# Revit family: EVC-1122-VI
name_source: partatom
category: Communication Devices
revit_build: Autodesk Revit 2017 (Build: 20160225_1515(x64)
units: mm (PartAtom-declared; Revit-internal decimal feet)

## family parameters
Always vertical = Yes
Cut with Voids When Loaded = No
Maintain Annotation Orientation = Yes
OmniClass Number = 23.85.10.11.11.21
OmniClass Title = Speakers
Part Type = Normal
Room Calculation Point = No
Round Connector Dimension = Use Diameter
Shared = No
Work Plane-Based = Yes

## types (2) — shared parameters
ArchitectsAndEngineersSpecs = https://www.electrovoice.com
Depth = 647.6 mm  [stored 2.12467 ft]
Description = 15-inch, two-way loudspeaker, with 90˚ x 55˚ constant directivity, rotatable waveguide. Power rating: 350 W Continuous, (1400 W Peak). Passive system: 98 dB, 129 dB maximum. Gland nut cover and stainless steel grille on PI versions. Optional high quality transformer and patented. Automatic Saturation Control (ASC) preserve low end in 70V/100V lines.
Disclaimer = http://resource.boschsecurity.com
IfcExportAs = IfcBuildingElementProxy
IfcExportType = IfcBuildingElementProxyType
InstallationManual = https://www.electrovoice.com
Length = 527.8 mm  [stored 1.73163 ft]
Manufacturer = Electro Voice
ManufacturerURL = https://www.electrovoice.com
PlanningTools = https://www.electrovoice.com
ProductInformation = https://www.electrovoice.com
Uniclass2015Code = Pr_60_75_08_02
Width = 411 mm  [stored 1.34843 ft]
zero-valued in all types: Default Elevation

## per-type parameters (varying)
| type | CTN | GrillMaterial | LoudspeakerMaterial | MaterialRALColour | ModelNumber |
| EVC1122VIW_12"_Speaker_White | EVC1122VIW | 16GA Powder-coatedGalvanneal - W | 13-plyWeather-resistantBirchEVCoat -RAL9010 | RAL9010 | F.01U.329.290 |
| EVC1122VIB_12"_Speaker_Black | EVC1122VIB | 16GA Powder-coatedGalvanneal - B | 13-plyWeather-resistantBirchEVCoat -RAL9004 | RAL9004 | F.01U.329.289 |

note: [stored X ft] marks values corroborated as IEEE doubles in the binary element streams (Revit-internal decimal feet)

## geometry (parser evidence)
native form markers: Sweep x12
no freeform markers — native parametric forms only
